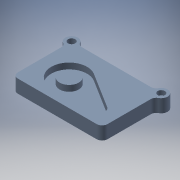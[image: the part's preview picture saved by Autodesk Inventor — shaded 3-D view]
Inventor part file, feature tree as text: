
AUTODESK INVENTOR PART (.ipt)
format: ipt  version: 2016 (Build 200138000, 138)  size: 280,576 bytes
history: native  units: mm
features: extrude x2, hole x2, sketch x2, fillet x1
ambient origin geometry x8: Origin, YZ Plane, XZ Plane, XY Plane, X Axis, Y Axis, Z Axis, Center Point
bodies: Solid1 (feature_tree)
feature tree (7):
  extrude  "Extrusion1"  Depth=132.0mm
  fillet  "Fillet1"  Radius=28.1556mm
  extrude  "Extrusion2"  Depth=12.0mm
  hole  "Hole1"  [1 undecoded]
  hole  "Hole2"  [1 undecoded]
  sketch  "Sketch1"  dims[d0=200.0mm d1=132.0mm d3=28.1556mm]
  sketch  "Sketch2"  dims[d4=29.2mm d5=0.0mm d6=12.0mm d7=42.66mm d8=60.0mm d9=66.6mm d10=80.0mm d12=93.2mm d13=26.6mm d15=13.2mm d16=0.0mm d36=10.0mm d37=10.0mm d19=5.0mm d20=6.0mm d21=16.0mm d22=13.2mm d23=90.0deg d24=8.0mm d25=20.594885mm d38=10.0mm d39=10.0mm d28=5.0mm d29=6.0mm d30=16.0mm d31=10.0mm d32=90.0deg d33=8.0mm d34=20.594885mm d35=200.0mm]
note: 2 required parameter values undecoded (feature->parameter linkage not recoverable at this tier; creation-order binding heuristic only, values carry confidence <= 0.55)
